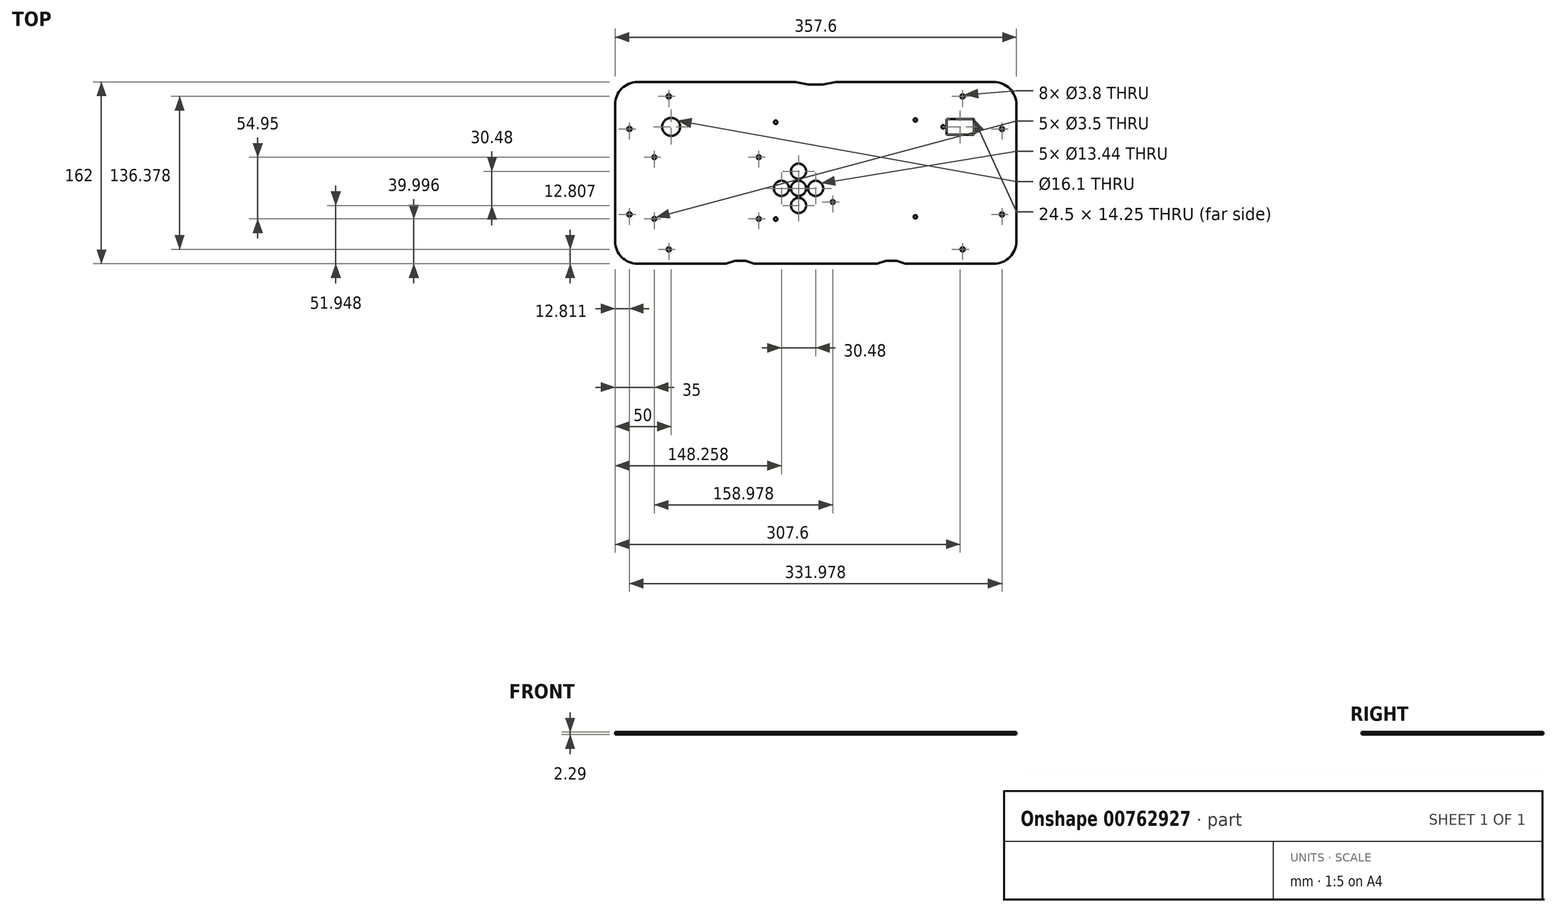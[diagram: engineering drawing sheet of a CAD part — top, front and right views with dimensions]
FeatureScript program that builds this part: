
annotation { "Feature Type Name" : "Feature", "Feature Type Description" : "" }
export const myFeature = defineFeature(function(context is Context, id is Id, definition is map)
    precondition{}
    {
        {
            var Q0;
            Q0=qCreatedBy(makeId("Top.planeOp"),FACE);
            var sketch = newSketch(context, id + "F0", { "sketchPlane" : qUnion([Q0])});
            skLineSegment(sketch, "E0.bottom", {"start": v(-158.73, 79.95) * mm, "end": v(-17.96, 79.95) * mm});
            skLineSegment(sketch, "E0.top", {"start": v(-158.73, -82.05) * mm, "end": v(-79.8, -82.05) * mm});
            skLineSegment(sketch, "E0.left", {"start": v(-178.8, 59.88) * mm, "end": v(-178.8, -61.99) * mm});
            skLineSegment(sketch, "E0.right", {"start": v(178.8, 59.88) * mm, "end": v(178.8, -61.99) * mm});
            skPoint(sketch, "E1.visualSharp", {"position": v(-178.8, 79.95) * mm});
            skArc(sketch, "E1.filletArc", {"start": v(-158.73, 79.95) * mm, "mid": v(-172.92, 74.07) * mm, "end": v(-178.8, 59.88) * mm});
            skPoint(sketch, "E2.visualSharp", {"position": v(-178.8, -82.05) * mm});
            skArc(sketch, "E2.filletArc", {"start": v(-178.8, -61.99) * mm, "mid": v(-172.92, -76.18) * mm, "end": v(-158.73, -82.05) * mm});
            skPoint(sketch, "E3.visualSharp", {"position": v(178.8, -82.05) * mm});
            skArc(sketch, "E3.filletArc", {"start": v(158.73, -82.05) * mm, "mid": v(172.92, -76.18) * mm, "end": v(178.8, -61.99) * mm});
            skPoint(sketch, "E4.visualSharp", {"position": v(178.8, 79.95) * mm});
            skArc(sketch, "E4.filletArc", {"start": v(178.8, 59.88) * mm, "mid": v(172.92, 74.07) * mm, "end": v(158.73, 79.95) * mm});
            skCircle(sketch, "E5", {"center": v(-130.9, 67.13) * mm, "radius": 1.9 * mm});
            skCircle(sketch, "E6", {"center": v(-165.99, 38.1) * mm, "radius": 1.9 * mm});
            skCircle(sketch, "E7", {"center": v(-165.99, -38.1) * mm, "radius": 1.9 * mm});
            skCircle(sketch, "E8", {"center": v(-130.9, -69.24) * mm, "radius": 1.9 * mm});
            skCircle(sketch, "E9.MirrorC", {"center": v(165.99, 38.1) * mm, "radius": 1.9 * mm});
            skCircle(sketch, "E10.MirrorC", {"center": v(130.9, 67.13) * mm, "radius": 1.9 * mm});
            skCircle(sketch, "E11.MirrorC", {"center": v(165.99, -38.1) * mm, "radius": 1.9 * mm});
            skCircle(sketch, "E12.MirrorC", {"center": v(130.9, -69.24) * mm, "radius": 1.9 * mm});
            skArc(sketch, "E13.0", {"start": v(-158.73, 60.9) * mm, "mid": v(-159.45, 60.6) * mm, "end": v(-159.75, 59.88) * mm});
            skLineSegment(sketch, "E13.1", {"start": v(-159.75, 59.88) * mm, "end": v(-159.75, -61.99) * mm, "construction": true});
            skLineSegment(sketch, "E13.2", {"start": v(-158.73, 60.9) * mm, "end": v(158.73, 60.9) * mm, "construction": true});
            skArc(sketch, "E13.3", {"start": v(-159.75, -61.99) * mm, "mid": v(-159.45, -62.7) * mm, "end": v(-158.73, -63) * mm});
            skArc(sketch, "E13.4", {"start": v(159.75, 59.88) * mm, "mid": v(159.45, 60.6) * mm, "end": v(158.73, 60.9) * mm});
            skLineSegment(sketch, "E13.5", {"start": v(159.75, 59.88) * mm, "end": v(159.75, -61.99) * mm, "construction": true});
            skArc(sketch, "E13.6", {"start": v(158.73, -63) * mm, "mid": v(159.45, -62.7) * mm, "end": v(159.75, -61.99) * mm});
            skLineSegment(sketch, "E13.7", {"start": v(-158.73, -63) * mm, "end": v(158.73, -63) * mm, "construction": true});
            skLineSegment(sketch, "E14", {"start": v(0, 79.95) * mm, "end": v(0, 0) * mm, "construction": true});
            skLineSegment(sketch, "E15", {"start": v(178.8, 0) * mm, "end": v(0, 0) * mm, "construction": true});
            skCircle(sketch, "E16", {"center": v(-128.8, 39.95) * mm, "radius": 8.05 * mm});
            skCircle(sketch, "E17", {"center": v(113.53, 39.95) * mm, "radius": 1.48 * mm});
            skLineSegment(sketch, "E18.bottom", {"start": v(116.55, 47.07) * mm, "end": v(141.05, 47.07) * mm});
            skLineSegment(sketch, "E18.top", {"start": v(116.55, 32.82) * mm, "end": v(141.05, 32.82) * mm});
            skLineSegment(sketch, "E18.left", {"start": v(116.55, 47.07) * mm, "end": v(116.55, 32.82) * mm});
            skLineSegment(sketch, "E18.right", {"start": v(141.05, 47.07) * mm, "end": v(141.05, 32.82) * mm});
            skLineSegment(sketch, "E19", {"start": v(141.05, 39.95) * mm, "end": v(116.55, 39.95) * mm, "construction": true});
            skCircle(sketch, "E20", {"center": v(144.08, 39.96) * mm, "radius": 1.48 * mm});
            skLineSegment(sketch, "E21", {"start": v(128.8, 47.07) * mm, "end": v(128.8, 32.82) * mm, "construction": true});
            skLineSegment(sketch, "E22", {"start": v(-6.5, 77.6) * mm, "end": v(6.5, 77.6) * mm});
            skLineSegment(sketch, "E23", {"start": v(0, 77.6) * mm, "end": v(0, 79.95) * mm, "construction": true});
            skLineSegment(sketch, "E24", {"start": v(6.5, 77.6) * mm, "end": v(17.96, 79.95) * mm});
            skLineSegment(sketch, "E25", {"start": v(-6.5, 77.6) * mm, "end": v(-17.96, 79.95) * mm});
            skLineSegment(sketch, "E26", {"start": v(17.96, 79.95) * mm, "end": v(158.73, 79.95) * mm});
            skPoint(sketch, "E27", {"position": v(-79.8, -82.05) * mm});
            skPoint(sketch, "E28", {"position": v(-54.8, -82.05) * mm});
            skLineSegment(sketch, "E29", {"start": v(-72.08, -79.45) * mm, "end": v(-62.52, -79.45) * mm});
            skLineSegment(sketch, "E30", {"start": v(-79.8, -82.05) * mm, "end": v(-72.08, -79.45) * mm});
            skLineSegment(sketch, "E31", {"start": v(-62.52, -79.45) * mm, "end": v(-54.8, -82.05) * mm});
            skLineSegment(sketch, "E32.trimOffspring", {"start": v(-54.8, -82.05) * mm, "end": v(54.8, -82.05) * mm});
            skPoint(sketch, "E33", {"position": v(79.8, -82.05) * mm});
            skPoint(sketch, "E34", {"position": v(54.8, -82.05) * mm});
            skLineSegment(sketch, "E35", {"start": v(62.52, -79.45) * mm, "end": v(72.08, -79.45) * mm});
            skLineSegment(sketch, "E36", {"start": v(79.8, -82.05) * mm, "end": v(72.08, -79.45) * mm});
            skLineSegment(sketch, "E37", {"start": v(54.8, -82.05) * mm, "end": v(62.52, -79.45) * mm});
            skLineSegment(sketch, "E38.trimOffspring", {"start": v(79.8, -82.05) * mm, "end": v(158.73, -82.05) * mm});
            skSolve(sketch);
        }
        {
            var Q0;
            Q0=makeQuery(id+"F0.imprint","IMPRINT",FACE,{"disambiguationData":[TD([[makeQuery(id+"F0.imprint","IMPRINT",EDGE,{"derivedFrom":sQuery(id+"F0.wireOp",EDGE,"E0.bottom")}),-1.0]])]});
            var sketch = newSketch(context, id + "F1", { "sketchPlane" : qUnion([Q0])});
            skLineSegment(sketch, "E39", {"start": v(91.38, -42.24) * mm, "end": v(91.38, -28.27) * mm, "construction": true});
            skLineSegment(sketch, "E40", {"start": v(91.38, -22.68) * mm, "end": v(91.38, 44.12) * mm, "construction": true});
            skLineSegment(sketch, "E41", {"start": v(88.84, 46.66) * mm, "end": v(-35.62, 46.66) * mm, "construction": true});
            skLineSegment(sketch, "E42", {"start": v(-38.16, 44.12) * mm, "end": v(-38.16, -42.24) * mm, "construction": true});
            skArc(sketch, "E43", {"start": v(91.38, 46.1) * mm, "mid": v(90.63, 47.9) * mm, "end": v(88.84, 48.64) * mm, "construction": true});
            skArc(sketch, "E44", {"start": v(88.84, -42.8) * mm, "mid": v(90.63, -42.06) * mm, "end": v(91.38, -40.26) * mm, "construction": true});
            skArc(sketch, "E45", {"start": v(-38.16, -42.05) * mm, "mid": v(-37.42, -43.85) * mm, "end": v(-35.62, -44.6) * mm, "construction": true});
            skArc(sketch, "E46", {"start": v(-35.62, 48.64) * mm, "mid": v(-37.42, 47.9) * mm, "end": v(-38.16, 46.1) * mm, "construction": true});
            skLineSegment(sketch, "E47", {"start": v(-35.62, -44.78) * mm, "end": v(88.84, -44.78) * mm, "construction": true});
            skArc(sketch, "E48", {"start": v(90.87, -21.21) * mm, "mid": v(91.23, -21.06) * mm, "end": v(91.38, -20.7) * mm, "construction": true});
            skArc(sketch, "E49", {"start": v(91.38, -26.3) * mm, "mid": v(91.23, -25.93) * mm, "end": v(90.87, -25.78) * mm, "construction": true});
            skArc(sketch, "E50", {"start": v(90.36, -25.28) * mm, "mid": v(90.51, -25.64) * mm, "end": v(90.87, -25.78) * mm, "construction": true});
            skArc(sketch, "E51", {"start": v(90.87, -21.21) * mm, "mid": v(90.51, -21.36) * mm, "end": v(90.36, -21.72) * mm, "construction": true});
            skLineSegment(sketch, "E52", {"start": v(90.36, -27.26) * mm, "end": v(90.36, -23.7) * mm, "construction": true});
            skCircle(sketch, "E53", {"center": v(88.84, -40.26) * mm, "radius": 1.55 * mm});
            skCircle(sketch, "E54", {"center": v(88.84, 46.1) * mm, "radius": 1.55 * mm});
            skCircle(sketch, "E55", {"center": v(-35.62, 44.12) * mm, "radius": 1.55 * mm});
            skCircle(sketch, "E56", {"center": v(-35.62, -42.24) * mm, "radius": 1.55 * mm});
            skCircle(sketch, "E57", {"center": v(-26.04, -14.86) * mm, "radius": 0.93 * mm, "construction": true});
            skCircle(sketch, "E58", {"center": v(-35.04, -14.86) * mm, "radius": 0.93 * mm, "construction": true});
            skCircle(sketch, "E59", {"center": v(4.44, -14.86) * mm, "radius": 0.93 * mm, "construction": true});
            skCircle(sketch, "E60", {"center": v(-4.56, -14.86) * mm, "radius": 0.93 * mm, "construction": true});
            skCircle(sketch, "E61", {"center": v(-15.3, -34.6) * mm, "radius": 0.93 * mm, "construction": true});
            skCircle(sketch, "E62", {"center": v(-15.3, -25.6) * mm, "radius": 0.93 * mm, "construction": true});
            skCircle(sketch, "E63", {"center": v(-15.3, -4.12) * mm, "radius": 0.93 * mm, "construction": true});
            skCircle(sketch, "E64", {"center": v(-15.3, 4.88) * mm, "radius": 0.93 * mm, "construction": true});
            skCircle(sketch, "E65", {"center": v(-10.8, -14.86) * mm, "radius": 0.93 * mm, "construction": true});
            skCircle(sketch, "E66", {"center": v(-19.8, -14.86) * mm, "radius": 0.93 * mm, "construction": true});
            skCircle(sketch, "E67", {"center": v(15.18, -27) * mm, "radius": 1.75 * mm});
            skLineSegment(sketch, "E68", {"start": v(-35.04, -14.86) * mm, "end": v(-26.04, -14.86) * mm, "construction": true});
            skLineSegment(sketch, "E69", {"start": v(-19.8, -14.86) * mm, "end": v(-10.8, -14.86) * mm, "construction": true});
            skLineSegment(sketch, "E70", {"start": v(-4.56, -14.86) * mm, "end": v(4.44, -14.86) * mm, "construction": true});
            skLineSegment(sketch, "E71", {"start": v(-15.3, -25.6) * mm, "end": v(-15.3, -34.6) * mm, "construction": true});
            skLineSegment(sketch, "E72", {"start": v(-15.3, 4.88) * mm, "end": v(-15.3, -4.12) * mm, "construction": true});
            skCircle(sketch, "E73", {"center": v(-30.54, -14.86) * mm, "radius": 6.72 * mm});
            skCircle(sketch, "E74", {"center": v(-15.3, -14.86) * mm, "radius": 6.72 * mm});
            skCircle(sketch, "E75", {"center": v(-15.3, 0.38) * mm, "radius": 6.72 * mm});
            skCircle(sketch, "E76", {"center": v(-0.06, -14.86) * mm, "radius": 6.72 * mm});
            skCircle(sketch, "E77", {"center": v(-15.3, -30.1) * mm, "radius": 6.72 * mm});
            skSolve(sketch);
        }
        {
            var Q0;
            Q0=makeQuery(id+"F0.imprint","IMPRINT",FACE,{"disambiguationData":[TD([[makeQuery(id+"F0.imprint","IMPRINT",EDGE,{"derivedFrom":sQuery(id+"F0.wireOp",EDGE,"E0.bottom")}),-1.0]])]});
            var sketch = newSketch(context, id + "F2", { "sketchPlane" : qUnion([Q0])});
            skLineSegment(sketch, "E78", {"start": v(-146.3, 15.45) * mm, "end": v(-48.25, 15.45) * mm, "construction": true});
            skLineSegment(sketch, "E79", {"start": v(-146.3, -44.6) * mm, "end": v(-48.25, -44.6) * mm, "construction": true});
            skLineSegment(sketch, "E80", {"start": v(-146.3, 15.45) * mm, "end": v(-146.3, -44.6) * mm, "construction": true});
            skLineSegment(sketch, "E81", {"start": v(-48.25, 15.45) * mm, "end": v(-48.25, -44.6) * mm, "construction": true});
            skLineSegment(sketch, "E82", {"start": v(-145.8, 5.2) * mm, "end": v(-48.75, 5.2) * mm, "construction": true});
            skLineSegment(sketch, "E83", {"start": v(-145.8, -34.5) * mm, "end": v(-48.75, -34.5) * mm, "construction": true});
            skLineSegment(sketch, "E84", {"start": v(-145.8, 5.2) * mm, "end": v(-145.8, -34.5) * mm, "construction": true});
            skLineSegment(sketch, "E85", {"start": v(-48.75, 5.2) * mm, "end": v(-48.75, -34.5) * mm, "construction": true});
            skCircle(sketch, "E86", {"center": v(-143.8, 12.9) * mm, "radius": 1.75 * mm});
            skCircle(sketch, "E87", {"center": v(-143.8, -42.05) * mm, "radius": 1.75 * mm});
            skCircle(sketch, "E88", {"center": v(-50.75, 12.9) * mm, "radius": 1.75 * mm});
            skCircle(sketch, "E89", {"center": v(-50.75, -42.05) * mm, "radius": 1.75 * mm});
            skLineSegment(sketch, "E90", {"start": v(-135.2, -1.55) * mm, "end": v(-59.2, -1.55) * mm, "construction": true});
            skLineSegment(sketch, "E91", {"start": v(-135.2, -27.8) * mm, "end": v(-59.2, -27.8) * mm, "construction": true});
            skLineSegment(sketch, "E92", {"start": v(-135.2, -1.55) * mm, "end": v(-135.2, -27.8) * mm, "construction": true});
            skLineSegment(sketch, "E93", {"start": v(-59.2, -1.55) * mm, "end": v(-59.2, -27.8) * mm, "construction": true});
            skSolve(sketch);
        }
        {
            var Q0;
            Q0=qSketchRegion(id+"F0",true);
            extrude(context, id + "F3", {"entities" : qUnion([Q0]), "depth" : 2.3 * mm, "offsetDistance" : 25 * mm});
        }
        {
            var Q0;
            Q0=qSketchRegion(id+"F2",true);
            extrude(context, id + "F4", {"entities" : qUnion([Q0]), "operationType" : NewBodyOperationType.REMOVE, "oppositeDirection" : true, "depth" : -2.3 * mm, "offsetDistance" : 25 * mm});
        }
        {
            var Q0;
            Q0=qSketchRegion(id+"F1",true);
            extrude(context, id + "F5", {"entities" : qUnion([Q0]), "operationType" : NewBodyOperationType.REMOVE, "oppositeDirection" : true, "depth" : -2.3 * mm, "offsetDistance" : 25 * mm});
        }
    });
